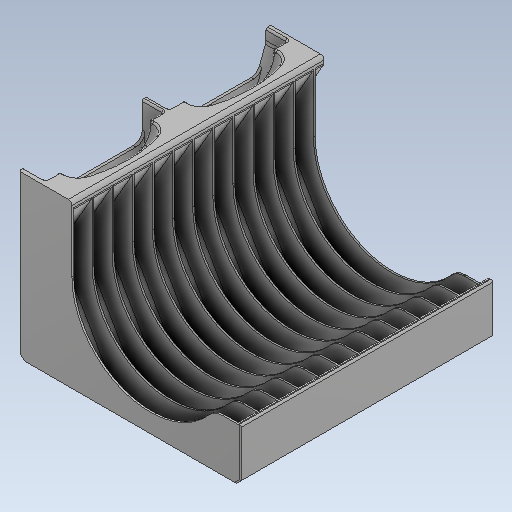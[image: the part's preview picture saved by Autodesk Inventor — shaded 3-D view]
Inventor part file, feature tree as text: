
AUTODESK INVENTOR PART (.ipt)
format: ipt  version: 2021 (Build 250183000, 183)  size: 823,808 bytes
history: native  units: mm
features: projected_geometry x9, extrude x8, sketch x7, fillet x3, chamfer x3, plane x2, other x2, pattern_linear x1, loft x1, mirror x1
ambient origin geometry x8: Origin, YZ Plane, XZ Plane, XY Plane, X Axis, Y Axis, Z Axis, Center Point
bodies: Solid1 (feature_tree)
feature tree (37):
  extrude  "Extrusion1"  Depth=0.25mm
  fillet  "Fillet1"  Radius=0.25mm
  extrude  "Extrusion2"  Depth=1.0mm
  pattern_linear  "Rectangular Pattern1"  Count1=3  [1 undecoded]
  extrude  "Extrusion3"  Depth=1.0mm
  chamfer  "Chamfer1"  Distance=32.0mm
  chamfer  "Chamfer2"  Distance=2.0mm
  chamfer  "Chamfer3"  Distance=13.0mm
  plane  "Work Plane1"
  sketch  "Sketch4"  dims[d9=125.0mm d10=30.0mm]
  extrude  "Extrusion4"  Depth=91.0mm
  extrude  "Extrusion5"  Depth=91.0mm
  extrude  "Extrusion6"  Depth=92.0mm
  extrude  "Extrusion7"  Depth=91.0mm
  extrude  "Extrusion8"  Depth=91.0mm
  plane  "Work Plane2"
  loft  "Loft1"
  fillet  "Fillet2"  Radius=21.24649mm
  mirror  "Mirror1"
  fillet  "Fillet3"  Radius=30.0mm
  sketch  "Sketch1"  dims[d0=108.4mm d1=0.25mm d2=0.25mm]
  sketch  "Sketch2"  dims[d4=1.0mm d5=0.25mm]
  projected_geometry  "Projected Loop1"
  sketch  "Sketch3"  dims[d6=11.126556mm]
  projected_geometry  "Projected Loop2"
  projected_geometry  "Projected Loop3"
  projected_geometry  "Projected Loop4"
  projected_geometry  "Projected Loop5"
  sketch  "Sketch5"  dims[d11=130.0mm d12=1.0mm]
  projected_geometry  "Projected Loop6"
  sketch  "Sketch6"  dims[d13=36.0mm]
  projected_geometry  "Projected Loop7"
  sketch  "Sketch7"  dims[d14=1.0mm d15=32.0mm d16=2.0mm d17=13.0mm d18=23.0mm d19=2.98813mm d20=92.0mm d21=106.0mm d22=38.0mm d23=32.373046mm d24=21.24649mm d25=30.0mm d26=142.5mm d27=0.0mm d28=1.0mm d29=0.0mm d30=130.0mm d32=11.344mm d33=10.0mm d34=8.0mm d35=30.0mm d36=54.0mm d37=8.0mm d38=44.0mm d39=6.0mm d40=0.0mm d41=2.0mm d42=3.0mm d43=2.0mm d44=45.0deg d45=0.75mm d46=2.0mm d47=45.0deg d48=0.5mm d49=2.0mm d50=45.0deg d51=-1.5mm d52=9.6mm d53=37.2mm d54=0.5mm d56=3.166667mm d57=81.4mm d60=0.5mm d61=65.5mm d62=0.5mm d63=59.65mm d64=135.0deg d65=20.0mm d66=0.0mm d67=0.0mm d68=9.0mm d69=0.0mm d70=10.5mm d71=0.0mm d72=0.5mm d73=1.0mm d74=2.0mm d75=50.0mm d76=10.5mm d77=32.0mm d78=1.0mm d79=0.0mm d81=8.0mm d82=65.0mm d83=1.0mm d84=0.0mm d85=7.0mm d86=0.0mm d87=90.0deg d88=0.0mm d89=90.0deg d90=0.0mm d91=90.0deg d92=1.583333mm d93=5.0mm d94=1.0mm d95=1.0mm d96=2.0mm d97=1.0mm d98=2.0mm d99=74.0mm d100=38.0mm d101=20.6mm d102=91.0mm]
  projected_geometry  "Projected Loop8"
  projected_geometry  "Projected Loop9"
  other  "Edges1"
  other  "Edges2"
note: 1 required parameter value undecoded (feature->parameter linkage not recoverable at this tier; creation-order binding heuristic only, values carry confidence <= 0.55)
